# Revit family: 1286xxx Ascoli Single switched CE
name_source: partatom
category: Lighting Fixtures
revit_build: Autodesk Revit 2018 (Build: 20170223_1515(x64)
units: mm (PartAtom-declared; Revit-internal decimal feet)

## family parameters
Always vertical = Yes
Cut with Voids When Loaded = No
Host = Wall
Light Source = No
OmniClass Number = 23.80.70.00
OmniClass Title = Lighting
Part Type = Normal
Room Calculation Point = No
Round Connector Dimension = Use Diameter
Shared = No

## types (4) — shared parameters
Dimmable = No
Driver Required = No
Efficacy (lm/w) = Lamp Dependant
Electrical Class = 2
IP rating = IP20
Lamp = GU10 LED
Main Material = Metal - Aluminium / Zinc
Manufacturer = Astro Lighting Ltd
Power (Watts) = 6W Max
Product CCT = Lamp Dependant
Product CRI = Lamp Dependant
Product Dimensions = 90 x 130 x 103 mm
Product Location = Wall
Product Name = Ascoli Single Switched
Product URL = https://www.astrolighting.com
Product Weight = 0.46 kg
URL = www.astrolighting.com

## per-type parameters (varying)
| type | Main Finish | Product SKU |
| Ascoli Single Switched Bronze | Bronze | 1286009 |
| Ascoli Single Switched Matt Black | Matt Black | 1286079 |
| Ascoli Single Switched Matt Nickel | Matt Nickel | 1286011 |
| Ascoli Single Switched Textured White | Textured White | 1286010 |

## geometry (parser evidence)
native form markers: Sweep x2
no freeform markers — native parametric forms only
